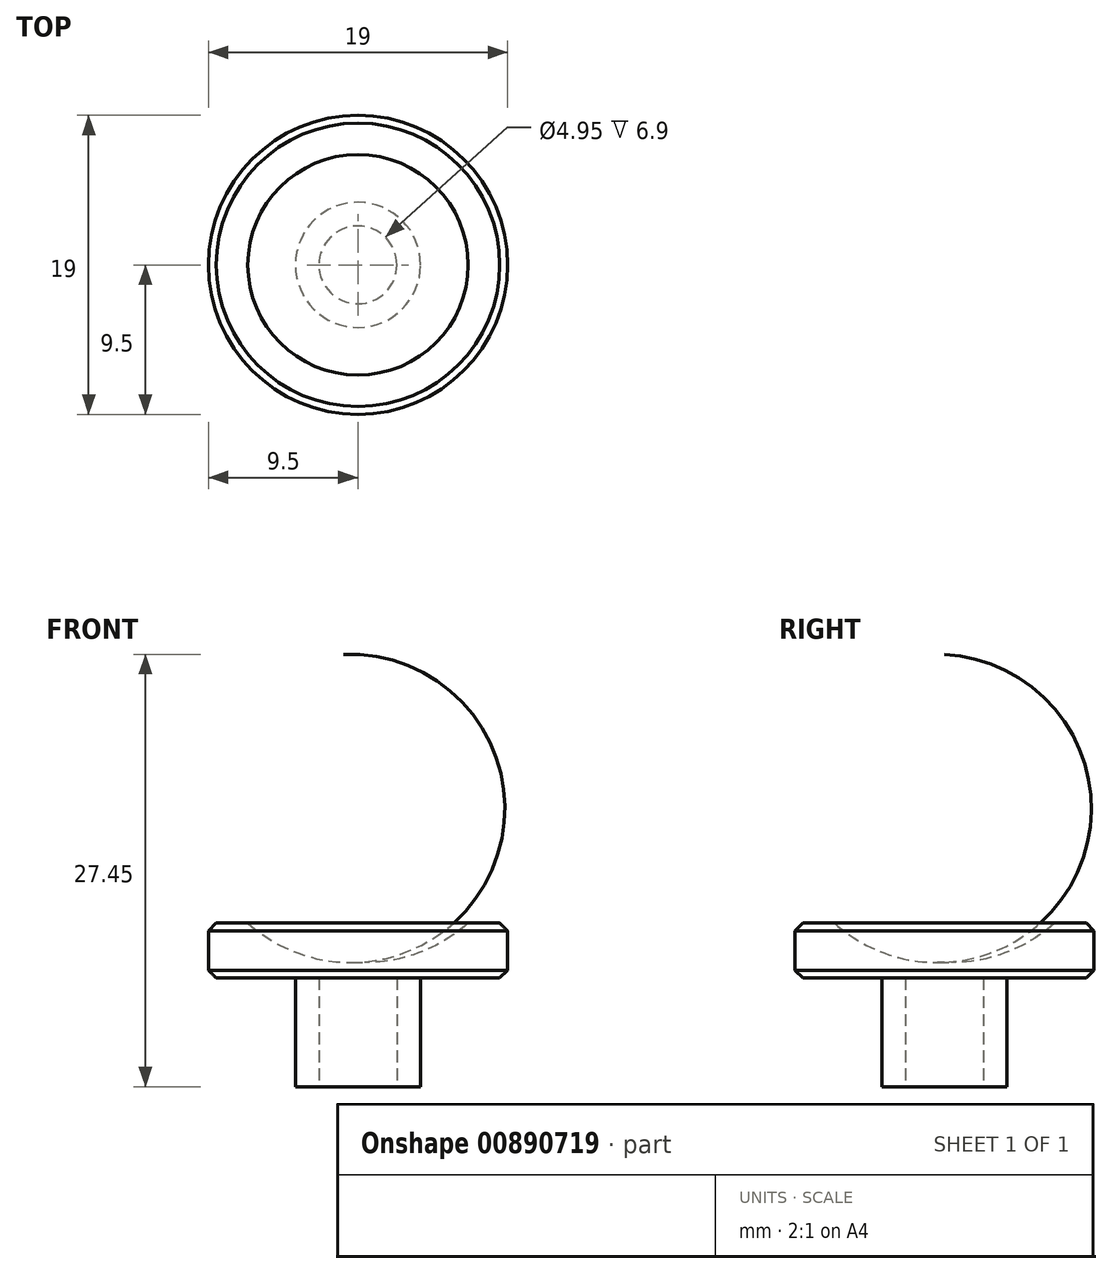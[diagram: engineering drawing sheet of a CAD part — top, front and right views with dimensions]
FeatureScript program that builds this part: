
annotation { "Feature Type Name" : "Feature", "Feature Type Description" : "" }
export const myFeature = defineFeature(function(context is Context, id is Id, definition is map)
    precondition{}
    {
        {
            var Q0;
            Q0=qCreatedBy(makeId("Front.planeOp"),FACE);
            var sketch = newSketch(context, id + "F0", { "sketchPlane" : qUnion([Q0])});
            skLineSegment(sketch, "E0", {"start": v(3.98, 0) * mm, "end": v(3.98, 6.9) * mm});
            skLineSegment(sketch, "E1", {"start": v(3.98, 6.9) * mm, "end": v(9.5, 6.9) * mm});
            skLineSegment(sketch, "E2", {"start": v(9.5, 6.9) * mm, "end": v(9.5, 10.4) * mm});
            skLineSegment(sketch, "E3", {"start": v(9.5, 10.4) * mm, "end": v(7, 10.4) * mm});
            skLineSegment(sketch, "E4", {"start": v(2.47, 6.9) * mm, "end": v(2.48, 0) * mm});
            skLineSegment(sketch, "E5", {"start": v(2.47, 6.9) * mm, "end": v(0, 6.9) * mm});
            skLineSegment(sketch, "E6", {"start": v(2.48, 0) * mm, "end": v(3.98, 0) * mm});
            skPoint(sketch, "E7", {"position": v(0, 7.9) * mm});
            skArc(sketch, "E8", {"start": v(0, 7.9) * mm, "mid": v(3.75, 8.46) * mm, "end": v(7, 10.4) * mm});
            skLineSegment(sketch, "E9", {"start": v(0, 6.9) * mm, "end": v(0, 7.9) * mm});
            skSolve(sketch);
        }
        {
            var Q0;
            Q0=makeQuery(id+"F0.imprint","IMPRINT",FACE,{"disambiguationData":[TD([[makeQuery(id+"F0.imprint","IMPRINT",EDGE,{"derivedFrom":sQuery(id+"F0.wireOp",EDGE,"E0")}),1.0]])]});
            var Q1;
            Q1=sQuery(id+"F0.wireOp",EDGE,"E9");
            revolve(context, id + "F1", {"surfaceOperationType" : NewSurfaceOperationType.NEW, "entities" : qUnion([Q0]), "axis" : qUnion([Q1]), "revolveType" : RevolveType.FULL});
        }
        {
            var Q0;
            Q0=makeQuery(id+"F1.opRevolve","SWEPT_EDGE",EDGE,{"disambiguationData":[OSD([sQuery(id+"F0.wireOp",EDGE,"E2"),sQuery(id+"F0.wireOp",EDGE,"E3")])]});
            var Q1;
            Q1=makeQuery(id+"F1.opRevolve","SWEPT_EDGE",EDGE,{"disambiguationData":[OSD([sQuery(id+"F0.wireOp",EDGE,"E1"),sQuery(id+"F0.wireOp",EDGE,"E2")])]});
            chamfer(context, id + "F2", {"entities" : qUnion([Q0, Q1]), "width" : 0.5 * mm, "tangentPropagation" : true});
        }
    });
